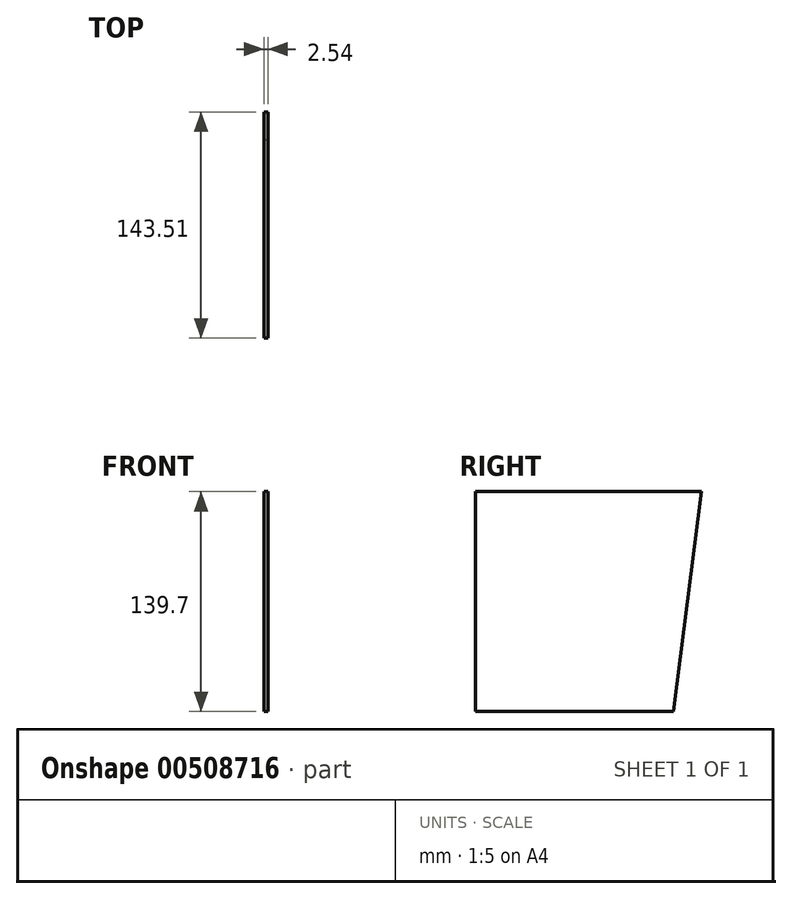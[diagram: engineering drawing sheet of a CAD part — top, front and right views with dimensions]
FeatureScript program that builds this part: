
annotation { "Feature Type Name" : "Feature", "Feature Type Description" : "" }
export const myFeature = defineFeature(function(context is Context, id is Id, definition is map)
    precondition{}
    {
        {
            var Q0;
            Q0=qCreatedBy(makeId("Front.planeOp"),FACE);
            var sketch = newSketch(context, id + "F0", { "sketchPlane" : qUnion([Q0])});
            skLineSegment(sketch, "E0.bottom", {"start": v(-52.56, 100.46) * mm, "end": v(-50.02, 100.46) * mm});
            skLineSegment(sketch, "E0.top", {"start": v(-52.56, -39.24) * mm, "end": v(-50.02, -39.24) * mm});
            skLineSegment(sketch, "E0.left", {"start": v(-52.56, 100.46) * mm, "end": v(-52.56, -39.24) * mm});
            skLineSegment(sketch, "E0.right", {"start": v(-50.02, 100.46) * mm, "end": v(-50.02, -39.24) * mm});
            skSolve(sketch);
        }
        {
            var Q0;
            Q0=makeQuery(id+"F0.imprint","IMPRINT",FACE,{"disambiguationData":[TD([[makeQuery(id+"F0.imprint","IMPRINT",EDGE,{"derivedFrom":sQuery(id+"F0.wireOp",EDGE,"E0.bottom")}),-1.0]])]});
            extrude(context, id + "F1", {"entities" : qUnion([Q0]), "depth" : 143.5 * mm});
        }
        {
            var Q0;
            Q0=makeQuery(id+"F1.opExtrude","SWEPT_FACE",FACE,{"disambiguationData":[OSD([sQuery(id+"F0.wireOp",EDGE,"E0.left")])]});
            var sketch = newSketch(context, id + "F2", { "sketchPlane" : qUnion([Q0])});
            skLineSegment(sketch, "E1", {"start": v(0, 100.46) * mm, "end": v(17.78, -39.24) * mm});
            skSolve(sketch);
        }
        {
            var Q0;
            {var subQ0=sQuery(id+"F2.wireOp",EDGE,"E1");Q0=makeQuery(id+"F2.imprint","IMPRINT",FACE,{"disambiguationData":[TD([[makeQuery(id+"F2.imprint","IMPRINT",EDGE,{"derivedFrom":subQ0}),-1.0]])]});}
            extrude(context, id + "F3", {"entities" : qUnion([Q0]), "operationType" : NewBodyOperationType.REMOVE, "oppositeDirection" : true, "depth" : 25.4 * mm});
        }
    });
